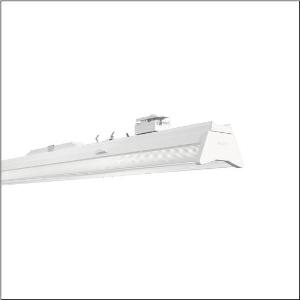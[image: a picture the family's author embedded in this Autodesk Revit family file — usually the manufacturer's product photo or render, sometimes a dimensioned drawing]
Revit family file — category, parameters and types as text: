
# Revit family: licross_11_performance_mo_51td16cn69xg
name_source: partatom
category: Lighting Fixtures
units: mm (PartAtom-declared; Revit-internal decimal feet)

## family parameters
Cut with Voids When Loaded = No
Host = Face
Light Source = No
Part Type = Normal
Room Calculation Point = No
Round Connector Dimension = Use Diameter
Shared = No

## types (1)
- --- (1 x LED, 8960 lm, 49.4 W, 6500K)
    Apparent Load = 49 VA
    CIE Flux Codes = 66 88 96 79 100
    Color Rendering = 80
    Color Temperature = 6500K
    Default Elevation = 1800 mm
    Description = Licross 11 Performance MO, luminaire insert, of sheet steel, galvanised, coil coated, white, length: 1.500mm, width: 120mm, height: 123mm, LED rated luminous flux: 8.960lm, light colour: 865, SDCM (Standard Deviation of Colour Matching)MacAdam ≤ 2 SDCM (initial), control gear: ON/OFF Multilumen, CLOi, with plug, 3-pole, with phase selection, mains connection: 220..240V, AC, 50/60Hz, start of lifetime: 49W, end of service life: 55W, internal wiring halogen-free, primary light control with lens, of plastic, primary optical cover: cover, of PMMA, light emission: direct/indirect distribution, primary light characteristic: symmetric, protection rating (complete): IP54, insulation class (complete): insulation class I (protective earthing), certification: CE, ENEC, VDE, UKCA, protection symbol: D if used in an environment with non-conductive dust loads with corresponding accessories, impact resistance: IK06, permissible ambient temperature for indoor applications: -35..+40°C, corresponds to IFS (International Featured Standards) requirements for safety and quality in the food industry, reducing of maximum allowable ambient temperature of 5°C with ceiling mounting, LABS conformity tested according to VDMA 24364:2018-05, The light source and the operating device comply with the requirements of the Ecodesign Regulation (EU) 2019/2020 and are replaceable in accordance with this regulation, packaging unit: 1 piece
    Height = 114 mm
    Lamp = 1 x LED
    Lamp Light Flux = 8960 lm
    Lamp Power = 49.4 W
    Lamp count = 1
    Length = 1500 mm
    Luminous efficacy = 181 lm/W
    Manufacturer = Siteco
    ModVariant = No
    Model = 51TD16CN69XG
    Mounting Place = Ceiling
    Mounting Type = Pendant
    Number of Poles = 1
    OnlyDefault = Yes
    Power Factor = 1
    Product Name = Licross 11 Performance MO
    Product group = luminaire insert | ceiling pendant
    ProductGroupID = 901
    Protection Class = Protection class I
    Protection Degree = IP 54
    RLX_Detail_Level = 1
    RLX_Emergency_Light_Flux = 0 lm
    RLX_Emergency_Type = 0
    RLX_Emergency_Type_DB = No
    RlxData = <blob elided: 32069 chars, md5=0ef12ebf>
    Socket = socket
    Standby Power = 0 W
    System Light Flux = 8960 lm
    System Power = 49 W
    Type Comments = factory setting: luminous flux: 100 % | (A | C | E) | 113 mA
    Type Image = l_1256138.jpg
    URL = http://relux.com
    VarID = @adj_000999
    Voltage = 0 V
    Weight = 0.00 kg
    Width = 120 mm

## geometry (parser evidence)
native form markers: Blend x4, Sweep x10
no freeform markers — native parametric forms only
